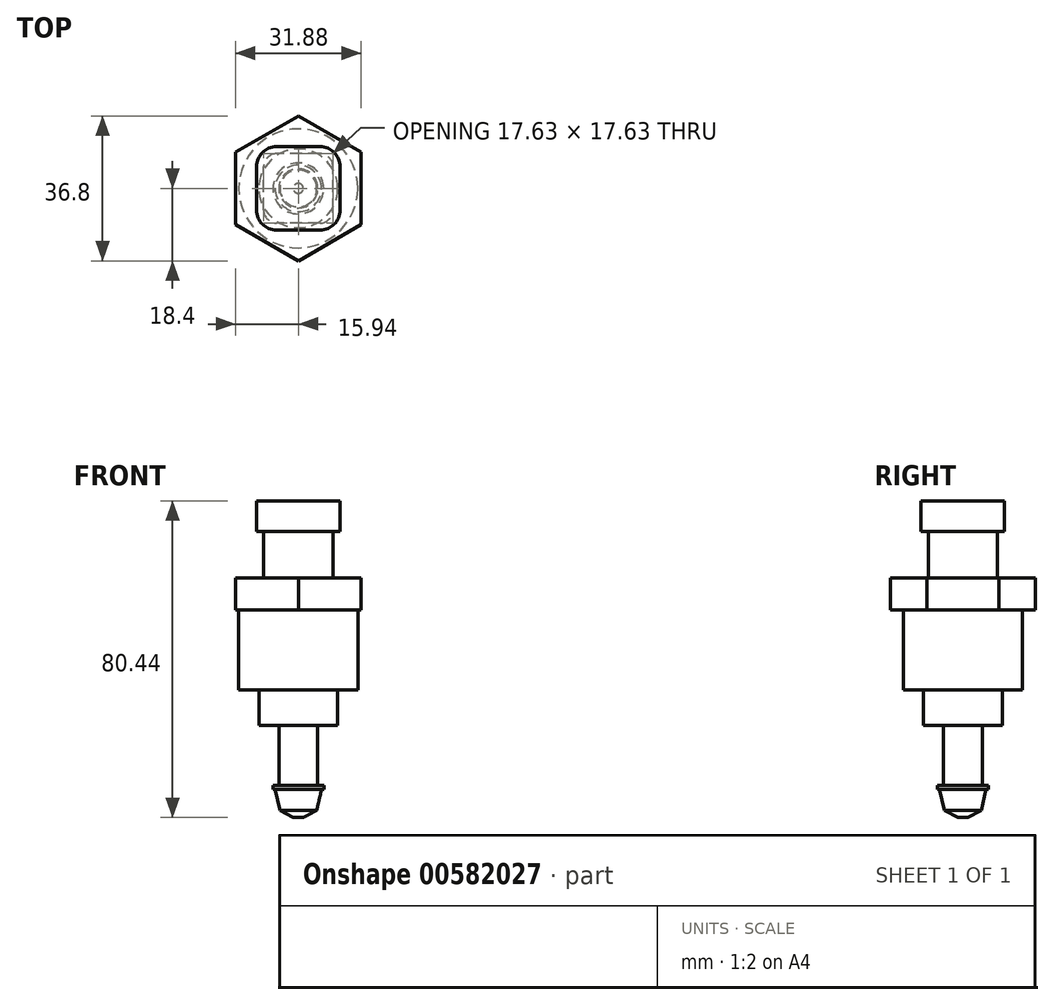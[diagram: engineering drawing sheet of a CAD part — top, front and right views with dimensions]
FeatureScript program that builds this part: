
annotation { "Feature Type Name" : "Feature", "Feature Type Description" : "" }
export const myFeature = defineFeature(function(context is Context, id is Id, definition is map)
    precondition{}
    {
        {
            var Q0;
            Q0=qCreatedBy(makeId("Top.planeOp"),FACE);
            var sketch = newSketch(context, id + "F0", { "sketchPlane" : qUnion([Q0])});
            skLineSegment(sketch, "E0.bottom", {"start": v(10.6, -10.6) * mm, "end": v(-10.6, -10.6) * mm});
            skLineSegment(sketch, "E0.top", {"start": v(10.6, 10.6) * mm, "end": v(-10.6, 10.6) * mm});
            skLineSegment(sketch, "E0.left", {"start": v(10.6, -10.6) * mm, "end": v(10.6, 10.6) * mm});
            skLineSegment(sketch, "E0.right", {"start": v(-10.6, -10.6) * mm, "end": v(-10.6, 10.6) * mm});
            skPoint(sketch, "E0.middle", {"position": v(0, 0) * mm});
            skSolve(sketch);
        }
        {
            var Q0;
            Q0 = qSketchRegion(id + "F0", true);
            extrude(context, id + "F1", {"entities" : qUnion([Q0]), "oppositeDirection" : true, "depth" : 7.75 * mm, "offsetDistance" : 25.4 * mm});
        }
        {
            var Q0;
            Q0=makeQuery(id+"F1.opExtrude","SWEPT_EDGE",EDGE,{"disambiguationData":[OSD([sQuery(id+"F0.wireOp",EDGE,"E0.bottom"),sQuery(id+"F0.wireOp",EDGE,"E0.left")])]});
            var Q1;
            Q1=makeQuery(id+"F1.opExtrude","SWEPT_EDGE",EDGE,{"disambiguationData":[OSD([sQuery(id+"F0.wireOp",EDGE,"E0.bottom"),sQuery(id+"F0.wireOp",EDGE,"E0.right")])]});
            var Q2;
            Q2=makeQuery(id+"F1.opExtrude","SWEPT_EDGE",EDGE,{"disambiguationData":[OSD([sQuery(id+"F0.wireOp",EDGE,"E0.top"),sQuery(id+"F0.wireOp",EDGE,"E0.right")])]});
            var Q3;
            Q3=makeQuery(id+"F1.opExtrude","SWEPT_EDGE",EDGE,{"disambiguationData":[OSD([sQuery(id+"F0.wireOp",EDGE,"E0.top"),sQuery(id+"F0.wireOp",EDGE,"E0.left")])]});
            fillet(context, id + "F2", {"entities" : qUnion([Q0, Q1, Q2, Q3]), "radius" : 5.08 * mm, "tangentPropagation" : true, "allowEdgeOverflow" : false});
        }
        {
            var Q0;
            Q0=makeQuery(id+"F1.opExtrude","CAP_FACE",FACE,{"disambiguationData":[OSD([sQuery(id+"F0.wireOp",EDGE,"E0.bottom"),sQuery(id+"F0.wireOp",EDGE,"E0.top"),sQuery(id+"F0.wireOp",EDGE,"E0.left"),sQuery(id+"F0.wireOp",EDGE,"E0.right")])],"isStart":false});
            var sketch = newSketch(context, id + "F3", { "sketchPlane" : qUnion([Q0])});
            skArc(sketch, "E1.0", {"start": v(8.81, 5.52) * mm, "mid": v(7.85, 7.85) * mm, "end": v(5.52, 8.81) * mm});
            skLineSegment(sketch, "E1.1", {"start": v(5.52, 8.81) * mm, "end": v(-5.52, 8.81) * mm});
            skLineSegment(sketch, "E1.2", {"start": v(8.81, 5.52) * mm, "end": v(8.81, -5.52) * mm});
            skArc(sketch, "E1.3", {"start": v(-5.52, 8.81) * mm, "mid": v(-7.85, 7.85) * mm, "end": v(-8.81, 5.52) * mm});
            skArc(sketch, "E1.4", {"start": v(5.52, -8.81) * mm, "mid": v(7.85, -7.85) * mm, "end": v(8.81, -5.52) * mm});
            skLineSegment(sketch, "E1.5", {"start": v(5.52, -8.81) * mm, "end": v(-5.52, -8.81) * mm});
            skArc(sketch, "E1.6", {"start": v(-8.81, -5.52) * mm, "mid": v(-7.85, -7.85) * mm, "end": v(-5.52, -8.81) * mm});
            skLineSegment(sketch, "E1.7", {"start": v(-8.81, 5.52) * mm, "end": v(-8.81, -5.52) * mm});
            skSolve(sketch);
        }
        {
            var Q0;
            Q0 = qSketchRegion(id + "F3", true);
            extrude(context, id + "F4", {"entities" : qUnion([Q0]), "operationType" : NewBodyOperationType.ADD, "depth" : 11.8 * mm, "offsetDistance" : 25.4 * mm});
        }
        {
            var Q0;
            Q0=makeQuery(id+"F4.opExtrude","CAP_FACE",FACE,{"disambiguationData":[OSD([sQuery(id+"F3.wireOp",EDGE,"E1.0"),sQuery(id+"F3.wireOp",EDGE,"E1.1"),sQuery(id+"F3.wireOp",EDGE,"E1.2"),sQuery(id+"F3.wireOp",EDGE,"E1.3"),sQuery(id+"F3.wireOp",EDGE,"E1.4"),sQuery(id+"F3.wireOp",EDGE,"E1.5"),sQuery(id+"F3.wireOp",EDGE,"E1.6"),sQuery(id+"F3.wireOp",EDGE,"E1.7")])],"isStart":false});
            var sketch = newSketch(context, id + "F5", { "sketchPlane" : qUnion([Q0])});
            skCircle(sketch, "E2.cCircle", {"center": v(0, 0) * mm, "radius": 15.94 * mm, "construction": true});
            skLineSegment(sketch, "E2.0", {"start": v(15.94, 9.2) * mm, "end": v(15.94, -9.2) * mm});
            skLineSegment(sketch, "E2.1", {"start": v(15.94, -9.2) * mm, "end": v(0, -18.4) * mm});
            skLineSegment(sketch, "E2.2", {"start": v(0, -18.4) * mm, "end": v(-15.94, -9.2) * mm});
            skLineSegment(sketch, "E2.3", {"start": v(-15.94, -9.2) * mm, "end": v(-15.94, 9.2) * mm});
            skLineSegment(sketch, "E2.4", {"start": v(-15.94, 9.2) * mm, "end": v(0, 18.4) * mm});
            skLineSegment(sketch, "E2.5", {"start": v(0, 18.4) * mm, "end": v(15.94, 9.2) * mm});
            skPoint(sketch, "E2.0.midPoint", {"position": v(15.94, 0) * mm});
            skSolve(sketch);
        }
        {
            var Q0;
            Q0 = qSketchRegion(id + "F5", true);
            extrude(context, id + "F6", {"entities" : qUnion([Q0]), "operationType" : NewBodyOperationType.ADD, "depth" : 8.1 * mm, "offsetDistance" : 25.4 * mm});
        }
        {
            var Q0;
            Q0=makeQuery(id+"F6.opExtrude","CAP_FACE",FACE,{"disambiguationData":[OSD([sQuery(id+"F5.wireOp",EDGE,"E2.0"),sQuery(id+"F5.wireOp",EDGE,"E2.1"),sQuery(id+"F5.wireOp",EDGE,"E2.2"),sQuery(id+"F5.wireOp",EDGE,"E2.3"),sQuery(id+"F5.wireOp",EDGE,"E2.4"),sQuery(id+"F5.wireOp",EDGE,"E2.5")])],"isStart":false});
            var sketch = newSketch(context, id + "F7", { "sketchPlane" : qUnion([Q0])});
            skCircle(sketch, "E3", {"center": v(0, 0) * mm, "radius": 15.11 * mm});
            skSolve(sketch);
        }
        {
            var Q0;
            Q0 = qSketchRegion(id + "F7", true);
            extrude(context, id + "F8", {"entities" : qUnion([Q0]), "operationType" : NewBodyOperationType.ADD, "depth" : 20.32 * mm, "offsetDistance" : 25.4 * mm});
        }
        {
            var Q0;
            Q0=makeQuery(id+"F8.opExtrude","CAP_FACE",FACE,{"disambiguationData":[OSD([sQuery(id+"F7.wireOp",EDGE,"E3")])],"isStart":false});
            var sketch = newSketch(context, id + "F9", { "sketchPlane" : qUnion([Q0])});
            skCircle(sketch, "E4", {"center": v(0, 0) * mm, "radius": 10 * mm});
            skSolve(sketch);
        }
        {
            var Q0;
            Q0 = qSketchRegion(id + "F9", true);
            extrude(context, id + "F10", {"entities" : qUnion([Q0]), "operationType" : NewBodyOperationType.ADD, "depth" : 9.02 * mm, "offsetDistance" : 25.4 * mm});
        }
        {
            var Q0;
            Q0=makeQuery(id+"F10.opExtrude","CAP_FACE",FACE,{"disambiguationData":[OSD([sQuery(id+"F9.wireOp",EDGE,"E4")])],"isStart":false});
            var sketch = newSketch(context, id + "F11", { "sketchPlane" : qUnion([Q0])});
            skCircle(sketch, "E5", {"center": v(0, 0) * mm, "radius": 4.95 * mm});
            skSolve(sketch);
        }
        {
            var Q0;
            Q0 = qSketchRegion(id + "F11", true);
            extrude(context, id + "F12", {"entities" : qUnion([Q0]), "operationType" : NewBodyOperationType.ADD, "depth" : 15.24 * mm, "offsetDistance" : 25.4 * mm});
        }
        {
            var Q0;
            Q0=makeQuery(id+"F12.opExtrude","CAP_FACE",FACE,{"disambiguationData":[OSD([sQuery(id+"F11.wireOp",EDGE,"E5")])],"isStart":false});
            var sketch = newSketch(context, id + "F13", { "sketchPlane" : qUnion([Q0])});
            skCircle(sketch, "E6", {"center": v(0, 0) * mm, "radius": 6.48 * mm});
            skSolve(sketch);
        }
        {
            var Q0;
            Q0 = qSketchRegion(id + "F13", true);
            extrude(context, id + "F14", {"entities" : qUnion([Q0]), "operationType" : NewBodyOperationType.ADD, "depth" : 1.04 * mm, "offsetDistance" : 25.4 * mm});
        }
        {
            var Q0;
            Q0=qCreatedBy(makeId("Front.planeOp"),FACE);
            var sketch = newSketch(context, id + "F15", { "sketchPlane" : qUnion([Q0])});
            skLineSegment(sketch, "E7", {"start": v(0, -73.28) * mm, "end": v(0, -80.44) * mm});
            skLineSegment(sketch, "E8", {"start": v(1.27, -80.44) * mm, "end": v(4.67, -78.61) * mm});
            skLineSegment(sketch, "E9", {"start": v(4.67, -78.61) * mm, "end": v(5.9, -73.28) * mm});
            skLineSegment(sketch, "E10", {"start": v(5.9, -73.28) * mm, "end": v(0, -73.28) * mm});
            skLineSegment(sketch, "E11", {"start": v(5.9, -73.28) * mm, "end": v(6.48, -73.28) * mm, "construction": true});
            skLineSegment(sketch, "E12", {"start": v(0, -80.44) * mm, "end": v(1.27, -80.44) * mm});
            skSolve(sketch);
        }
        {
            var Q0;
            Q0=makeQuery(id+"F15.imprint","IMPRINT",FACE,{"disambiguationData":[TD([[makeQuery(id+"F15.imprint","IMPRINT",EDGE,{"derivedFrom":sQuery(id+"F15.wireOp",EDGE,"E7")}),1.0]])]});
            var Q1;
            Q1=sQuery(id+"F15.wireOp",EDGE,"E7");
            revolve(context, id + "F16", {"operationType" : NewBodyOperationType.ADD, "entities" : qUnion([Q0]), "axis" : qUnion([Q1]), "revolveType" : RevolveType.FULL});
        }
    });
